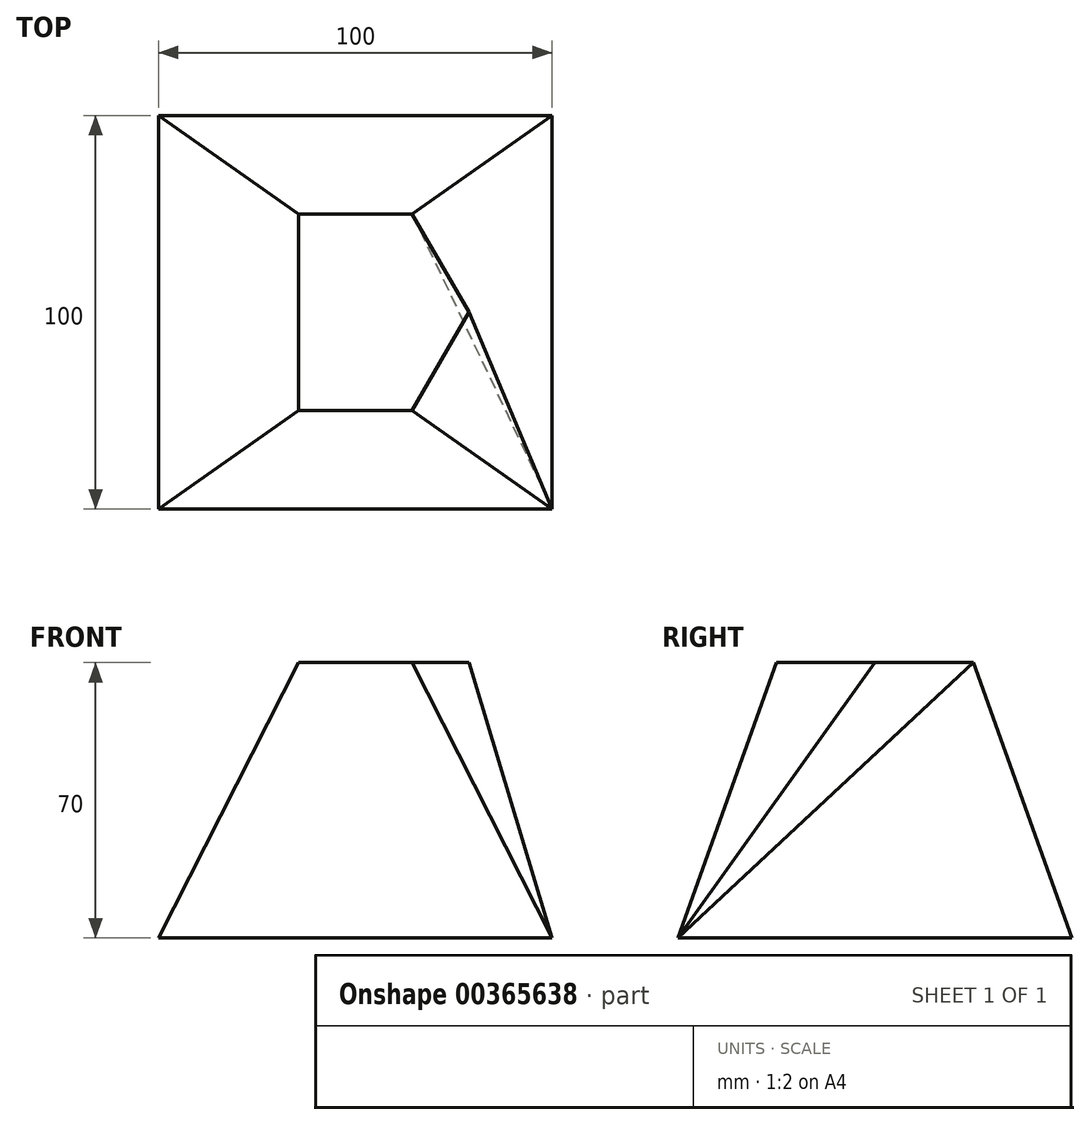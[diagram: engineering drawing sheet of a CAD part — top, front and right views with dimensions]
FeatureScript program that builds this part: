
annotation { "Feature Type Name" : "Feature", "Feature Type Description" : "" }
export const myFeature = defineFeature(function(context is Context, id is Id, definition is map)
    precondition{}
    {
        {
            var Q0;
            Q0=qCreatedBy(makeId("Top.planeOp"),FACE);
            var sketch = newSketch(context, id + "F0", { "sketchPlane" : qUnion([Q0])});
            skLineSegment(sketch, "E0.bottom", {"start": v(50, -50) * mm, "end": v(-50, -50) * mm});
            skLineSegment(sketch, "E0.top", {"start": v(50, 50) * mm, "end": v(-50, 50) * mm});
            skLineSegment(sketch, "E0.left", {"start": v(50, -50) * mm, "end": v(50, 50) * mm});
            skLineSegment(sketch, "E0.right", {"start": v(-50, -50) * mm, "end": v(-50, 50) * mm});
            skPoint(sketch, "E0.middle", {"position": v(0, 0) * mm});
            skSolve(sketch);
        }
        {
            var Q0;
            Q0=qCreatedBy(makeId("Top.planeOp"),FACE);
            cPlane(context, id + "F1", {"entities" : qUnion([Q0]), "cplaneType" : CPlaneType.OFFSET, "offset" : 70 * mm, "width" : 150 * mm, "height" : 150 * mm});
        }
        {
            var Q0;
            Q0=qCreatedBy(id+"F1.planeOp",FACE);
            var sketch = newSketch(context, id + "F2", { "sketchPlane" : qUnion([Q0])});
            skCircle(sketch, "E1.cCircle", {"center": v(0, 0) * mm, "radius": 28.87 * mm, "construction": true});
            skLineSegment(sketch, "E1.0", {"start": v(28.87, 0) * mm, "end": v(14.43, -25) * mm});
            skLineSegment(sketch, "E1.1", {"start": v(14.43, -25) * mm, "end": v(-14.43, -25) * mm});
            skLineSegment(sketch, "E1.2", {"start": v(-14.43, -25) * mm, "end": v(-28.87, 0) * mm});
            skLineSegment(sketch, "E1.3", {"start": v(-28.87, 0) * mm, "end": v(-14.43, 25) * mm});
            skLineSegment(sketch, "E1.4", {"start": v(-14.43, 25) * mm, "end": v(14.43, 25) * mm});
            skLineSegment(sketch, "E1.5", {"start": v(14.43, 25) * mm, "end": v(28.87, 0) * mm});
            skLineSegment(sketch, "E2", {"start": v(-14.43, 25) * mm, "end": v(-14.43, -25) * mm});
            skLineSegment(sketch, "E3", {"start": v(14.43, 25) * mm, "end": v(14.43, -25) * mm});
            skSolve(sketch);
        }
        {
            var Q0;
            Q0=makeQuery(id+"F0.imprint","IMPRINT",FACE,{"disambiguationData":[TD([[makeQuery(id+"F0.imprint","IMPRINT",EDGE,{"derivedFrom":sQuery(id+"F0.wireOp",EDGE,"E0.bottom")}),-1.0]])]});
            var Q1;
            Q1=makeQuery(id+"F2.imprint","IMPRINT",FACE,{"disambiguationData":[TD([[makeQuery(id+"F2.imprint","IMPRINT",EDGE,{"derivedFrom":sQuery(id+"F2.wireOp",EDGE,"E1.1")}),-1.0]])]});
            loft(context, id + "F3", {"sheetProfilesArray" : [{ "sheetProfileEntities" : qUnion([Q0]) }, { "sheetProfileEntities" : qUnion([Q1]) }]});
        }
        {
            var Q1;
            Q1=makeQuery(id+"F2.imprint","IMPRINT",FACE,{"disambiguationData":[TD([[makeQuery(id+"F2.imprint","IMPRINT",EDGE,{"derivedFrom":sQuery(id+"F2.wireOp",EDGE,"E1.0")}),-1.0]])]});
            var Q2;
            Q2=makeQuery(id+"F3.opLoft","MID_CAP_VERTEX",VERTEX,{"disambiguationData":[OSD([sQuery(id+"F0.wireOp",EDGE,"E0.bottom"),sQuery(id+"F0.wireOp",EDGE,"E0.left")])],"capPos":0.0});
            loft(context, id + "F4", {"operationType" : NewBodyOperationType.ADD, "sheetProfilesArray" : [{ "sheetProfileEntities" : qUnion([Q1]) }, { "sheetProfileEntities" : qUnion([Q2]) }]});
        }
    });
